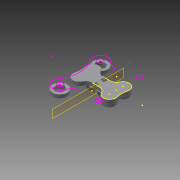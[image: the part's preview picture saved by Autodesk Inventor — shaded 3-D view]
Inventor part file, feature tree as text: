
AUTODESK INVENTOR PART (.ipt)
format: ipt  version: 2014 (Build 180170000, 170)  size: 579,584 bytes
history: native  units: in
note: dims shown in document units (in); Inventor stores cm internally (conversion verified against a paired STEP export)
features: fillet x8, extrude x7, sketch x7, chamfer x2, plane x1, mirror x1
ambient origin geometry x8: Origin, YZ Plane, XZ Plane, XY Plane, X Axis, Y Axis, Z Axis, Center Point
bodies: Body1 (feature_tree)
feature tree (26):
  extrude  "Extrusion12"  Depth=1.0441in
  extrude  "Extrusion13"  Depth=0.7874in
  sketch  "Sketch13"  dims[d2=1.5748in d65=0.7874in]
  plane  "Work Plane2"
  extrude  "Extrusion14"  Depth=0.5512in
  extrude  "Extrusion15"  TaperAngle=0.0deg  [1 undecoded]
  mirror  "Mirror2"
  extrude  "Extrusion16"  Depth=0.3346in
  extrude  "Extrusion17"  Depth=1.1811in TaperAngle=0.0deg
  extrude  "Extrusion18"  Depth=0.0197in TaperAngle=0.0deg
  chamfer  "Chamfer1"  Distance=0.0394in
  chamfer  "Chamfer2"  Distance=0.1181in
  fillet  "Fillet8"  Radius=0.1575in
  fillet  "Fillet9"  Radius=0.1575in
  fillet  "Fillet10"  Radius=0.2362in
  fillet  "Fillet11"  Radius=0.4724in
  fillet  "Fillet12"  Radius=0.1417in
  fillet  "Fillet13"  Radius=1.8898in
  fillet  "Fillet14"  Radius=0.5906in
  fillet  "Fillet15"  Radius=0.2362in
  sketch  "Sketch12"  dims[d0=1.1713in d1=1.0441in]
  sketch  "Sketch14"  dims[d70=0.2362in d71=0.0in d72=0.5512in]
  sketch  "Sketch15"  dims[d73=0.2362in d74=0.0in d75=0.0in]
  sketch  "Sketch16"  dims[d76=0.5945in d77=0.3346in]
  sketch  "Sketch17"  dims[d78=0.1181in d79=1.1811in d80=0.0in]
  sketch  "Sketch18"  dims[d81=0.0591in d82=0.1181in d83=0.0in d84=0.0394in d85=0.1181in d86=0.0in d87=0.1575in d88=0.1575in d89=0.2362in d90=0.0in d91=0.4724in d92=0.1417in d93=1.8898in d94=0.5906in d95=0.2362in d96=0.0in d97=0.0787in d98=0.0787in d99=45.0deg d100=0.0787in d101=0.0787in d102=45.0deg d103=0.0394in d104=0.0394in d105=0.0394in d106=0.0197in d107=0.0197in d108=0.0197in d109=0.0197in d110=0.0197in d112=0.3543in d113=1.9685in]
note: 1 required parameter value undecoded (feature->parameter linkage not recoverable at this tier; creation-order binding heuristic only, values carry confidence <= 0.55)
